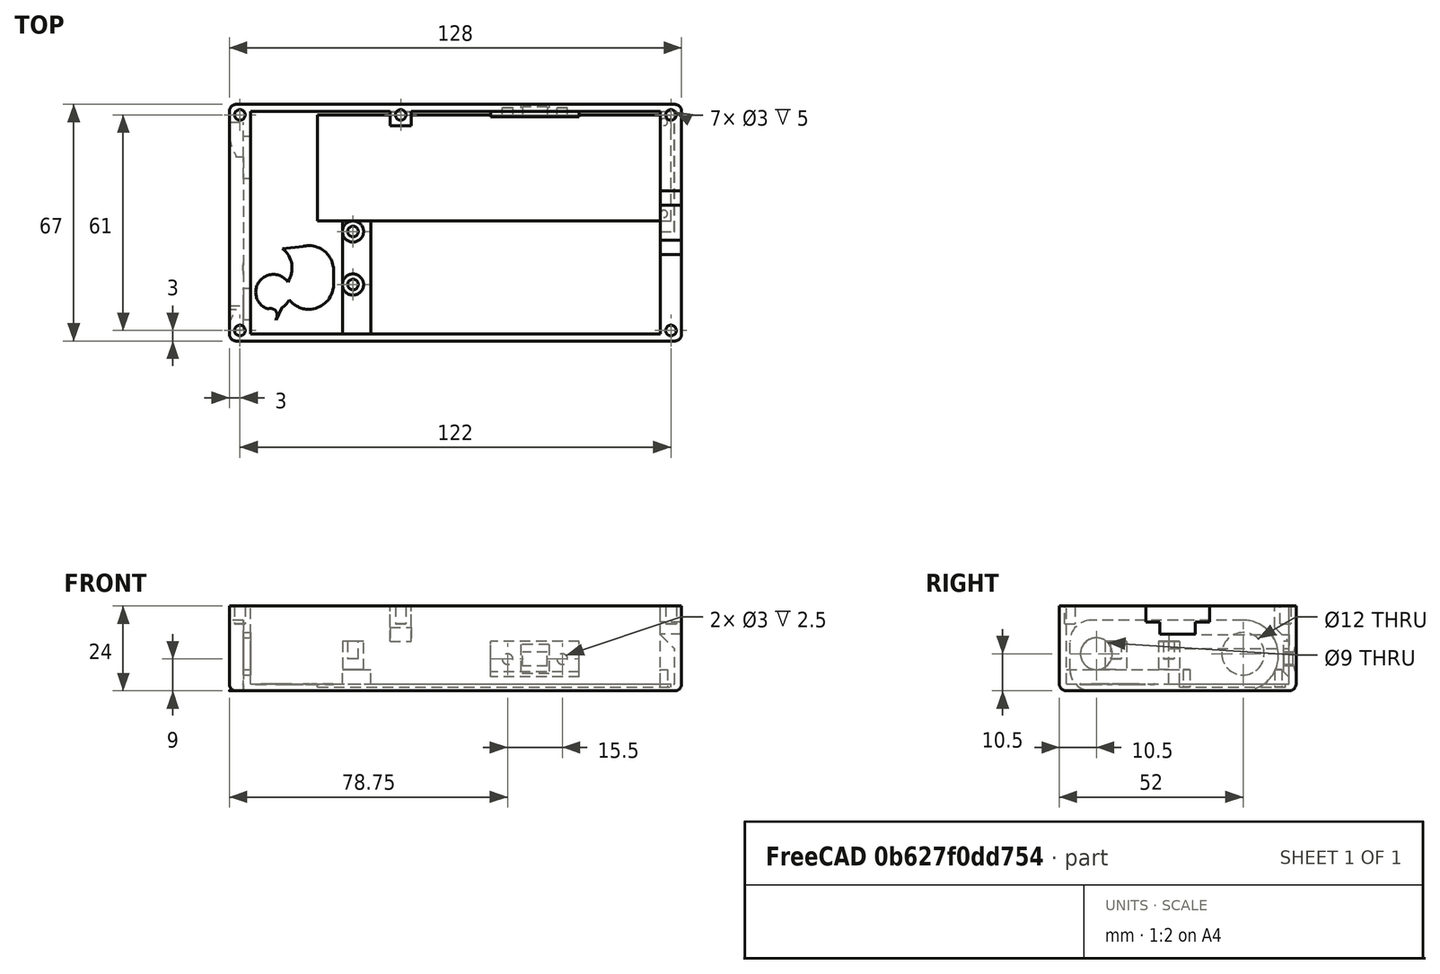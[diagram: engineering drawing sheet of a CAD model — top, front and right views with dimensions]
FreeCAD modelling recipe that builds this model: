
FCSTD DOCUMENT  (FreeCAD 1.0R39319 (Git))
Label: caseBottomV3
License: All rights reserved
LicenseURL: https://en.wikipedia.org/wiki/All_rights_reserved
objects: PartDesign::SubtractiveCylinder×19, PartDesign::SubtractiveBox×11, PartDesign::AdditiveCylinder×6, PartDesign::AdditiveBox×4, PartDesign::Chamfer×3, PartDesign::SubtractivePrism×1, PartDesign::Fillet×1, PartDesign::Body×1
note: 136 computed .brp shape members not serialized (recipe doc carries the construction recipe); baked Part::Feature solids carry a one-line shape summary decoded from their .brp

FEATURE [PartDesign::AdditiveBox] Box  label="base"
  AttacherType = Attacher::AttachEngine3D
  Height = 24
  Length = 128
  Refine = true
  Suppressed = false
  Width = 67
FEATURE [PartDesign::SubtractiveBox] Box001  label="primaryHollow"
  AttacherType = Attacher::AttachEngine3D
  AttachmentOffset = pos=(6,2,-22) rot=(0,0,1;0rad)
  AttachmentSupport = -> [Box]
  BaseFeature = -> Box
  Height = 22
  Length = 116
  MapMode = 5
  Placement = pos=(6,2,2) rot=(0,0,1;0rad)
  Refine = true
  Suppressed = false
  Width = 63
FEATURE [PartDesign::SubtractiveBox] Box002  label="batteryPCBRearNotch"
  AttacherType = Attacher::AttachEngine3D
  AttachmentOffset = pos=(116,29,0) rot=(0,0,1;0rad)
  AttachmentSupport = -> [Box001]
  BaseFeature = -> Box001
  Height = 10
  Length = 4
  MapMode = 5
  Placement = pos=(122,31,2) rot=(0,0,1;0rad)
  Refine = true
  Suppressed = false
  Width = 34
FEATURE [PartDesign::SubtractiveBox] Box003  label="batteryPCBRecess"
  AttacherType = Attacher::AttachEngine3D
  AttachmentOffset = pos=(-97,3,-1) rot=(0,0,1;0rad)
  AttachmentSupport = -> [Box002]
  BaseFeature = -> Box002
  Height = 1
  Length = 100
  MapMode = 5
  Placement = pos=(25,34,1) rot=(0,0,1;0rad)
  Refine = true
  Suppressed = false
  Width = 30
FEATURE [PartDesign::AdditiveBox] Box004  label="DACRearStand"
  AttacherType = Attacher::AttachEngine3D
  AttachmentOffset = pos=(7,-32,1) rot=(0,0,1;0rad)
  AttachmentSupport = -> [Box003]
  BaseFeature = -> Box003
  Height = 4
  Length = 8
  MapMode = 2
  Placement = pos=(32,2,2) rot=(0,0,1;0rad)
  Refine = true
  Suppressed = false
  Width = 32
FEATURE [PartDesign::AdditiveCylinder] Cylinder  label="DACLeftScrewSupport"
  Angle = 360
  AttacherType = Attacher::AttachEngine3D
  AttachmentOffset = pos=(3,14,0) rot=(0,0,1;0rad)
  AttachmentSupport = -> [Box004]
  BaseFeature = -> Box004
  FirstAngle = 0
  Height = 8
  MapMode = 5
  Placement = pos=(35,16,6) rot=(0,0,1;0rad)
  Radius = 3
  Refine = true
  SecondAngle = 0
  Suppressed = false
FEATURE [PartDesign::AdditiveCylinder] Cylinder001  label="DACRightScrewSupport"
  Angle = 360
  AttacherType = Attacher::AttachEngine3D
  AttachmentOffset = pos=(0,15,0) rot=(0,0,1;0rad)
  AttachmentSupport = -> [Cylinder]
  BaseFeature = -> Cylinder
  FirstAngle = 0
  Height = 8
  MapMode = 5
  Placement = pos=(35,31,6) rot=(0,0,1;0rad)
  Radius = 3
  Refine = true
  SecondAngle = 0
  Suppressed = false
FEATURE [PartDesign::SubtractiveCylinder] Cylinder002  label="DACRightScrewHollow"
  Angle = 360
  AttacherType = Attacher::AttachEngine3D
  AttachmentOffset = pos=(0,0,-5) rot=(0,0,1;0rad)
  AttachmentSupport = -> [Cylinder001]
  BaseFeature = -> Cylinder001
  FirstAngle = 0
  Height = 5
  MapMode = 5
  Placement = pos=(35,31,9) rot=(0,0,1;0rad)
  Radius = 1.5
  Refine = true
  SecondAngle = 0
  Suppressed = false
FEATURE [PartDesign::SubtractiveCylinder] Cylinder003  label="DACLefttScrewHollow"
  Angle = 360
  AttacherType = Attacher::AttachEngine3D
  AttachmentOffset = pos=(0,-15,0) rot=(0,0,1;0rad)
  AttachmentSupport = -> [Cylinder002]
  BaseFeature = -> Cylinder002
  FirstAngle = 0
  Height = 5
  MapMode = 5
  Placement = pos=(35,16,9) rot=(0,0,1;0rad)
  Radius = 1.5
  Refine = true
  SecondAngle = 0
  Suppressed = false
FEATURE [PartDesign::SubtractiveBox] Box005  label="DACInset"
  AttacherType = Attacher::AttachEngine3D
  AttachmentOffset = pos=(-36,-9,-4) rot=(0,0,1;0rad)
  AttachmentSupport = -> [Cylinder003]
  BaseFeature = -> Cylinder003
  Height = 4
  Length = 42
  MapMode = 5
  Placement = pos=(4,52,0) rot=(0.57735,-0.57735,-0.57735;2.0944rad)
  Refine = true
  Suppressed = false
  Width = 20
FEATURE [PartDesign::SubtractiveCylinder] Cylinder004  label="headphoneHole"
  Angle = 360
  AttacherType = Attacher::AttachEngine3D
  AttachmentOffset = pos=(41.5,10.5,-6) rot=(0,0,1;0rad)
  AttachmentSupport = -> [Box005]
  BaseFeature = -> Box005
  FirstAngle = 0
  Height = 6
  MapMode = 5
  Placement = pos=(6,10.5,10.5) rot=(0.57735,-0.57735,-0.57735;2.0944rad)
  Radius = 4.5
  Refine = true
  SecondAngle = 0
  Suppressed = false
FEATURE [PartDesign::SubtractiveCylinder] Cylinder005  label="volumePotHole"
  Angle = 360
  AttacherType = Attacher::AttachEngine3D
  AttachmentOffset = pos=(-41.5,0,-2) rot=(0,0,1;0rad)
  AttachmentSupport = -> [Cylinder004]
  BaseFeature = -> Cylinder004
  FirstAngle = 0
  Height = 6
  MapMode = 5
  Placement = pos=(6,52,10.5) rot=(0.57735,-0.57735,-0.57735;2.0944rad)
  Radius = 6
  Refine = true
  SecondAngle = 0
  Suppressed = false
FEATURE [PartDesign::SubtractiveCylinder] Cylinder006  label="volumeKnobRecess"
  Angle = 360
  AttacherType = Attacher::AttachEngine3D
  AttachmentOffset = pos=(0,-0.5,0) rot=(0,0,1;0rad)
  AttachmentSupport = -> [Cylinder005]
  BaseFeature = -> Cylinder005
  FirstAngle = 0
  Height = 4
  MapMode = 5
  Placement = pos=(4,52,10) rot=(0.57735,-0.57735,-0.57735;2.0944rad)
  Radius = 10
  Refine = true
  SecondAngle = 0
  Suppressed = false
FEATURE [PartDesign::SubtractiveCylinder] Cylinder007  label="headphoneRecess1"
  Angle = 360
  AttacherType = Attacher::AttachEngine3D
  AttachmentOffset = pos=(43,-4,0) rot=(0,0,1;0rad)
  AttachmentSupport = -> [Cylinder006]
  BaseFeature = -> Cylinder006
  FirstAngle = 0
  Height = 4
  MapMode = 2
  Placement = pos=(4,9,6) rot=(0.57735,-0.57735,-0.57735;2.0944rad)
  Radius = 6
  Refine = true
  SecondAngle = 0
  Suppressed = false
FEATURE [PartDesign::SubtractiveCylinder] Cylinder008  label="headphoneRecess2"
  Angle = 360
  AttacherType = Attacher::AttachEngine3D
  AttachmentOffset = pos=(0,8,0) rot=(0,0,1;0rad)
  AttachmentSupport = -> [Cylinder007]
  BaseFeature = -> Cylinder007
  FirstAngle = 0
  Height = 4
  MapMode = 5
  Placement = pos=(4,9,14) rot=(0.57735,-0.57735,-0.57735;2.0944rad)
  Radius = 6
  Refine = true
  SecondAngle = 0
  Suppressed = false
FEATURE [PartDesign::SubtractiveBox] Box006  label="headphoneRecess3"
  AttacherType = Attacher::AttachEngine3D
  AttachmentOffset = pos=(2,-8,0) rot=(0,0,1;0rad)
  AttachmentSupport = -> [Cylinder008]
  BaseFeature = -> Cylinder008
  Height = 4
  Length = 4
  MapMode = 5
  Placement = pos=(4,7,6) rot=(0.57735,-0.57735,-0.57735;2.0944rad)
  Refine = true
  Suppressed = false
  Width = 8
FEATURE [PartDesign::SubtractiveBox] Box007  label="headphoneRecess4"
  AttacherType = Attacher::AttachEngine3D
  AttachmentOffset = pos=(-8,8,0) rot=(0,0,1;0rad)
  AttachmentSupport = -> [Box006]
  BaseFeature = -> Box006
  Height = 4
  Length = 6
  MapMode = 5
  Placement = pos=(4,15,14) rot=(0.57735,-0.57735,-0.57735;2.0944rad)
  Refine = true
  Suppressed = false
  Width = 6
FEATURE [PartDesign::AdditiveBox] Box008  label="powerSwitchBase"
  AttacherType = Attacher::AttachEngine3D
  AttachmentOffset = pos=(-10,-95,0) rot=(0,0,1;0rad)
  AttachmentSupport = -> [Box007]
  BaseFeature = -> Box007
  Height = 1.5
  Length = 10
  MapMode = 5
  Placement = pos=(99,65,4) rot=(0.57735,-0.57735,0.57735;2.0944rad)
  Refine = true
  Suppressed = false
  Width = 25
FEATURE [PartDesign::SubtractiveBox] Box009
  AttacherType = Attacher::AttachEngine3D
  AttachmentOffset = pos=(3,9,-6) rot=(0,0,1;0rad)
  AttachmentSupport = -> [Box008]
  BaseFeature = -> Box008
  Height = 6
  Length = 4
  MapMode = 5
  Placement = pos=(90,69.5,7) rot=(0.57735,-0.57735,0.57735;2.0944rad)
  Refine = true
  Suppressed = false
  Width = 7
FEATURE [PartDesign::SubtractiveCylinder] Cylinder009
  Angle = 360
  AttacherType = Attacher::AttachEngine3D
  AttachmentOffset = pos=(2,11.25,-2.5) rot=(0,0,1;0rad)
  AttachmentSupport = -> [Box009]
  BaseFeature = -> Box009
  FirstAngle = 0
  Height = 2.5
  MapMode = 5
  Placement = pos=(78.75,66,9) rot=(0.57735,-0.57735,0.57735;2.0944rad)
  Radius = 1.5
  Refine = true
  SecondAngle = 0
  Suppressed = false
FEATURE [PartDesign::SubtractiveCylinder] Cylinder010
  Angle = 360
  AttacherType = Attacher::AttachEngine3D
  AttachmentOffset = pos=(0,-15.5,-2.5) rot=(0,0,1;0rad)
  AttachmentSupport = -> [Cylinder009]
  BaseFeature = -> Cylinder009
  FirstAngle = 0
  Height = 2.5
  MapMode = 5
  Placement = pos=(94.25,66,9) rot=(0.57735,-0.57735,0.57735;2.0944rad)
  Radius = 1.5
  Refine = true
  SecondAngle = 0
  Suppressed = false
FEATURE [PartDesign::SubtractiveBox] Box010
  AttacherType = Attacher::AttachEngine3D
  AttachmentOffset = pos=(-5,19.5,-4.5) rot=(0,0,1;0rad)
  BaseFeature = -> Cylinder010
  Height = 4.5
  Length = 6
  MapMode = 5
  Placement = pos=(128,42.5,19.5) rot=(0,0,1;3.14159rad)
  Refine = true
  Suppressed = false
  Width = 18
FEATURE [PartDesign::SubtractiveBox] Box011
  AttacherType = Attacher::AttachEngine3D
  AttachmentOffset = pos=(0,4,-3.5) rot=(0,0,1;0rad)
  AttachmentSupport = -> [Box010]
  BaseFeature = -> Box010
  Height = 3.5
  Length = 6
  MapMode = 5
  Placement = pos=(128,38.5,16) rot=(0,0,1;3.14159rad)
  Refine = true
  Suppressed = false
  Width = 10
FEATURE [PartDesign::AdditiveCylinder] Cylinder011
  Angle = 360
  AttacherType = Attacher::AttachEngine3D
  AttachmentOffset = pos=(5,2.5,0) rot=(0,0,1;0rad)
  AttachmentSupport = -> [Box011]
  BaseFeature = -> Box011
  FirstAngle = 0
  Height = 5
  MapMode = 5
  Placement = pos=(123,36,1) rot=(0,0,1;3.14159rad)
  Radius = 1
  Refine = true
  SecondAngle = 0
  Suppressed = false
FEATURE [PartDesign::AdditiveCylinder] Cylinder012
  Angle = 360
  AttacherType = Attacher::AttachEngine3D
  AttachmentOffset = pos=(0,-26,0) rot=(0,0,1;0rad)
  AttachmentSupport = -> [Cylinder011]
  BaseFeature = -> Cylinder011
  FirstAngle = 0
  Height = 5
  MapMode = 5
  Placement = pos=(123,62,1) rot=(0,0,1;3.14159rad)
  Radius = 1
  Refine = true
  SecondAngle = 0
  Suppressed = false
FEATURE [PartDesign::SubtractiveCylinder] Cylinder013
  Angle = 360
  AttacherType = Attacher::AttachEngine3D
  AttachmentOffset = pos=(40.5,8,8) rot=(0,-1,0;1.5708rad)
  AttachmentSupport = -> [Cylinder012]
  BaseFeature = -> Cylinder012
  FirstAngle = 0
  Height = 8
  MapMode = 5
  Placement = pos=(82.5,75,9) rot=(0.57735,0.57735,0.57735;2.0944rad)
  Radius = 9
  Refine = true
  SecondAngle = 0
  Suppressed = false
FEATURE [PartDesign::SubtractiveCylinder] Cylinder014
  Angle = 360
  AttacherType = Attacher::AttachEngine3D
  AttachmentOffset = pos=(72,-79.5,-5) rot=(0,0,1;0rad)
  AttachmentSupport = -> [Cylinder013]
  BaseFeature = -> Cylinder013
  FirstAngle = 0
  Height = 5
  MapMode = 5
  Placement = pos=(3,3,19) rot=(0,0,-1;1.5708rad)
  Radius = 1.5
  Refine = true
  SecondAngle = 0
  Suppressed = false
FEATURE [PartDesign::SubtractiveCylinder] Cylinder015
  Angle = 360
  AttacherType = Attacher::AttachEngine3D
  AttachmentOffset = pos=(-61,0,-5) rot=(0,0,1;0rad)
  AttachmentSupport = -> [Cylinder014]
  BaseFeature = -> Cylinder014
  FirstAngle = 0
  Height = 5
  MapMode = 5
  Placement = pos=(3,64,19) rot=(0,0,-1;1.5708rad)
  Radius = 1.5
  Refine = true
  SecondAngle = 0
  Suppressed = false
FEATURE [PartDesign::SubtractiveCylinder] Cylinder016
  Angle = 360
  AttacherType = Attacher::AttachEngine3D
  AttachmentOffset = pos=(0,122,-5) rot=(0,0,1;0rad)
  AttachmentSupport = -> [Cylinder015]
  BaseFeature = -> Cylinder015
  FirstAngle = 0
  Height = 5
  MapMode = 5
  Placement = pos=(125,64,19) rot=(0,0,-1;1.5708rad)
  Radius = 1.5
  Refine = true
  SecondAngle = 0
  Suppressed = false
FEATURE [PartDesign::SubtractiveCylinder] Cylinder017
  Angle = 360
  AttacherType = Attacher::AttachEngine3D
  AttachmentOffset = pos=(61,0,-5) rot=(0,0,1;0rad)
  AttachmentSupport = -> [Cylinder016]
  BaseFeature = -> Cylinder016
  FirstAngle = 0
  Height = 5
  MapMode = 5
  Placement = pos=(125,3,19) rot=(0,0,-1;1.5708rad)
  Radius = 1.5
  Refine = true
  SecondAngle = 0
  Suppressed = false
FEATURE [PartDesign::AdditiveBox] Box012
  AttacherType = Attacher::AttachEngine3D
  AttachmentOffset = pos=(-62,-79.5,-10) rot=(0,0,1;0rad)
  AttachmentSupport = -> [Cylinder017]
  BaseFeature = -> Cylinder017
  Height = 10
  Length = 4
  MapMode = 5
  Placement = pos=(45.5,65,14) rot=(0,0,-1;1.5708rad)
  Refine = true
  Suppressed = false
  Width = 6
FEATURE [PartDesign::SubtractiveCylinder] Cylinder018
  Angle = 360
  AttacherType = Attacher::AttachEngine3D
  AttachmentOffset = pos=(1,3,-5) rot=(0,0,1;0rad)
  AttachmentSupport = -> [Box012]
  BaseFeature = -> Box012
  FirstAngle = 0
  Height = 5
  MapMode = 5
  Placement = pos=(48.5,64,19) rot=(0,0,-1;1.5708rad)
  Radius = 1.5
  Refine = true
  SecondAngle = 0
  Suppressed = false
FEATURE [PartDesign::Chamfer] Chamfer
  Angle = 45
  Base = -> Cylinder018 [Edge114]
  BaseFeature = -> Cylinder018
  ChamferType = 0
  FlipDirection = false
  Placement = pos=(48.5,64,19) rot=(0,0,-1;1.5708rad)
  Refine = true
  Size = 3.9
  Size2 = 1
  SupportTransform = false
  Suppressed = false
  UseAllEdges = false
FEATURE [PartDesign::Chamfer] Chamfer001
  Angle = 45
  Base = -> Chamfer [Edge54]
  BaseFeature = -> Chamfer
  ChamferType = 0
  FlipDirection = false
  Placement = pos=(48.5,64,19) rot=(0,0,-1;1.5708rad)
  Refine = true
  Size = 3.9
  Size2 = 1
  SupportTransform = false
  Suppressed = false
  UseAllEdges = false
FEATURE [PartDesign::Chamfer] Chamfer002
  Angle = 45
  Base = -> Chamfer001 [Edge77]
  BaseFeature = -> Chamfer001
  ChamferType = 0
  FlipDirection = false
  Placement = pos=(48.5,64,19) rot=(0,0,-1;1.5708rad)
  Refine = true
  Size = 1.4
  Size2 = 1
  SupportTransform = false
  Suppressed = false
  UseAllEdges = false
FEATURE [PartDesign::SubtractiveCylinder] Cylinder019
  Angle = 360
  AttacherType = Attacher::AttachEngine3D
  AttachmentOffset = pos=(50,-36,-0.2) rot=(0,0,1;0rad)
  AttachmentSupport = -> [Chamfer002]
  BaseFeature = -> Chamfer002
  FirstAngle = 0
  Height = 0.2
  MapMode = 5
  Placement = pos=(12.5,14,1.8) rot=(0,0,-1;1.5708rad)
  Radius = 5
  Refine = true
  SecondAngle = 0
  Suppressed = false
FEATURE [PartDesign::SubtractiveCylinder] Cylinder020
  Angle = 360
  AttacherType = Attacher::AttachEngine3D
  AttachmentOffset = pos=(-2,10,-0.2) rot=(0,0,1;0rad)
  AttachmentSupport = -> [Cylinder019]
  BaseFeature = -> Cylinder019
  FirstAngle = 0
  Height = 0.2
  MapMode = 5
  Placement = pos=(22.5,16,1.8) rot=(0,0,-1;1.5708rad)
  Radius = 7
  Refine = true
  SecondAngle = 0
  Suppressed = false
FEATURE [PartDesign::SubtractiveCylinder] Cylinder021
  Angle = 360
  AttacherType = Attacher::AttachEngine3D
  AttachmentOffset = pos=(-4,0,0) rot=(0,0,1;0rad)
  AttachmentSupport = -> [Cylinder020]
  BaseFeature = -> Cylinder020
  FirstAngle = 0
  Height = 0.2
  MapMode = 5
  Placement = pos=(22.5,20,1.8) rot=(0,0,-1;1.5708rad)
  Radius = 7
  Refine = true
  SecondAngle = 0
  Suppressed = false
FEATURE [PartDesign::SubtractiveBox] Box013
  AttacherType = Attacher::AttachEngine3D
  AttachmentOffset = pos=(-1,2,0) rot=(0,0,1;0rad)
  AttachmentSupport = -> [Cylinder021]
  BaseFeature = -> Cylinder021
  Height = 0.2
  Length = 6
  MapMode = 2
  Placement = pos=(24.5,21,1.8) rot=(0,0,-1;1.5708rad)
  Refine = true
  Suppressed = false
  Width = 5
FEATURE [PartDesign::SubtractiveBox] Box014
  AttacherType = Attacher::AttachEngine3D
  AttachmentOffset = pos=(-5.1,-10.3,-0.2) rot=(0,0,1;0.10472rad)
  AttachmentSupport = -> [Box013]
  BaseFeature = -> Box013
  Height = 0.2
  Length = 4
  MapMode = 5
  Placement = pos=(14.2,26.1,1.8) rot=(0,0,-1;1.46608rad)
  Refine = true
  Suppressed = false
  Width = 9
FEATURE [PartDesign::AdditiveCylinder] Cylinder022
  Angle = 360
  AttacherType = Attacher::AttachEngine3D
  AttachmentOffset = pos=(5,-4,-0.2) rot=(0,0,1;0rad)
  AttachmentSupport = -> [Box014]
  BaseFeature = -> Box014
  FirstAngle = 0
  Height = 0.2
  MapMode = 5
  Placement = pos=(10.7446,20.7093,1.8) rot=(0,0,-1;1.46608rad)
  Radius = 7
  Refine = true
  SecondAngle = 0
  Suppressed = false
FEATURE [PartDesign::SubtractiveCylinder] Cylinder023
  Angle = 360
  AttacherType = Attacher::AttachEngine3D
  AttachmentOffset = pos=(7,1,0) rot=(0,0,1;0rad)
  AttachmentSupport = -> [Cylinder022]
  BaseFeature = -> Cylinder022
  FirstAngle = 0
  Height = 0.2
  MapMode = 5
  Placement = pos=(12.4708,13.8522,1.8) rot=(0,0,-1;1.46608rad)
  Radius = 5
  Refine = true
  SecondAngle = 0
  Suppressed = false
FEATURE [PartDesign::SubtractivePrism] Prism
  AttacherType = Attacher::AttachEngine3D
  AttachmentOffset = pos=(5.5,0,-0.2) rot=(0,0,1;0rad)
  AttachmentSupport = -> [Cylinder023]
  BaseFeature = -> Cylinder023
  Circumradius = 2.5
  FirstAngle = 0
  Height = 0.2
  MapMode = 5
  Placement = pos=(13.0457,8.38228,1.8) rot=(0,0,-1;1.46608rad)
  Polygon = 3
  Refine = true
  SecondAngle = 0
  Suppressed = false
FEATURE [PartDesign::AdditiveCylinder] Cylinder024
  Angle = 360
  AttacherType = Attacher::AttachEngine3D
  AttachmentOffset = pos=(0.9,-1.5,0) rot=(0,0,1;0rad)
  AttachmentSupport = -> [Prism]
  BaseFeature = -> Prism
  FirstAngle = 0
  Height = 0.2
  MapMode = 5
  Placement = pos=(11.648,7.33042,1.8) rot=(0,0,-1;1.46608rad)
  Radius = 1.9
  Refine = true
  SecondAngle = 0
  Suppressed = false
FEATURE [PartDesign::Fillet] Fillet
  Base = -> Cylinder024 [Edge119,Edge118,Edge105,Edge129,Edge127,Edge126,Edge120,Edge106,Edge104]
  BaseFeature = -> Cylinder024
  Placement = pos=(11.648,7.33042,1.8) rot=(0,0,-1;1.46608rad)
  Radius = 2
  Refine = true
  SupportTransform = false
  Suppressed = false
  UseAllEdges = false
FEATURE [PartDesign::Body] Body
  AllowCompound = false
  Group = -> [Box,Box001,Box002,Box003,Box004,Cylinder,Cylinder001,Cylinder002,Cylinder003,Box005,Cylinder004,Cylinder005,Cylinder006,Cylinder007,Cylinder008,Box006,Box007,Box008,Box009,Cylinder009,Cylinder010,Box010,Box011,Cylinder011,Cylinder012,Cylinder013,Cylinder014,Cylinder015,Cylinder016,Cylinder017,Box012,Cylinder018,Chamfer,Chamfer001,Chamfer002,Cylinder019,Cylinder020,Cylinder021,Box013,Box014,+5 more]
  Origin = -> Origin
  Tip = -> Fillet
